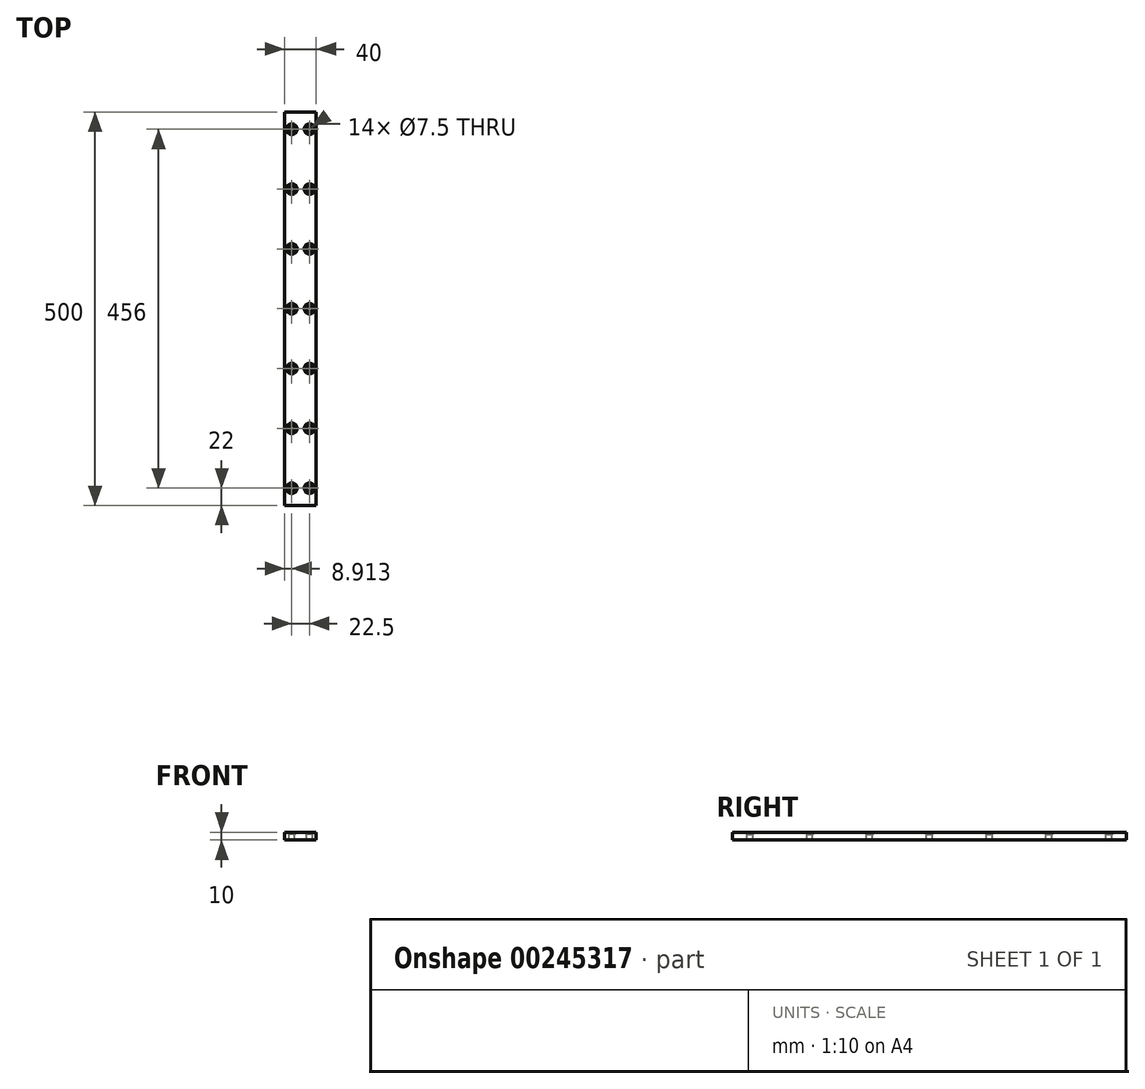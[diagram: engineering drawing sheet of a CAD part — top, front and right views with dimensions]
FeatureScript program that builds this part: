
annotation { "Feature Type Name" : "Feature", "Feature Type Description" : "" }
export const myFeature = defineFeature(function(context is Context, id is Id, definition is map)
    precondition{}
    {
        {
            var Q0;
            Q0=qCreatedBy(makeId("Front.planeOp"),FACE);
            var sketch = newSketch(context, id + "F0", { "sketchPlane" : qUnion([Q0])});
            skLineSegment(sketch, "E0.top", {"start": v(0, 434.89) * mm, "end": v(34.8, 434.89) * mm});
            skLineSegment(sketch, "E1.bottom", {"start": v(0, 0) * mm, "end": v(40, 0) * mm});
            skLineSegment(sketch, "E1.top", {"start": v(0, 10) * mm, "end": v(40, 10) * mm});
            skLineSegment(sketch, "E1.left", {"start": v(0, 0) * mm, "end": v(0, 10) * mm});
            skLineSegment(sketch, "E1.right", {"start": v(40, 0) * mm, "end": v(40, 10) * mm});
            skSolve(sketch);
        }
        {
            var Q0;
            Q0 = qSketchRegion(id + "F0", true);
            extrude(context, id + "F1", {"entities" : qUnion([Q0]), "depth" : 500 * mm, "offsetDistance" : 25 * mm});
        }
        {
            var Q0;
            Q0=makeQuery(id+"F1.opExtrude","SWEPT_FACE",FACE,{"disambiguationData":[OSD([sQuery(id+"F0.wireOp",EDGE,"E1.top")])]});
            var sketch = newSketch(context, id + "F2", { "sketchPlane" : qUnion([Q0])});
            skPoint(sketch, "E2", {"position": v(8.91, -22) * mm});
            skPoint(sketch, "E3.0.1.0", {"position": v(8.91, -98) * mm});
            skPoint(sketch, "E3.0.2.0", {"position": v(8.91, -174) * mm});
            skPoint(sketch, "E3.0.3.0", {"position": v(8.91, -250) * mm});
            skPoint(sketch, "E3.0.4.0", {"position": v(8.91, -326) * mm});
            skPoint(sketch, "E3.0.5.0", {"position": v(8.91, -402) * mm});
            skPoint(sketch, "E3.0.6.0", {"position": v(8.91, -478) * mm});
            skPoint(sketch, "E3.1.0.0", {"position": v(31.41, -22) * mm});
            skPoint(sketch, "E3.1.1.0", {"position": v(31.41, -98) * mm});
            skPoint(sketch, "E3.1.2.0", {"position": v(31.41, -174) * mm});
            skPoint(sketch, "E3.1.3.0", {"position": v(31.41, -250) * mm});
            skPoint(sketch, "E3.1.4.0", {"position": v(31.41, -326) * mm});
            skPoint(sketch, "E3.1.5.0", {"position": v(31.41, -402) * mm});
            skPoint(sketch, "E3.1.6.0", {"position": v(31.41, -478) * mm});
            skLineSegment(sketch, "E3.direction1", {"start": v(8.91, -22) * mm, "end": v(31.41, -22) * mm, "construction": true});
            skLineSegment(sketch, "E3.direction2", {"start": v(8.91, -22) * mm, "end": v(8.91, -98) * mm, "construction": true});
            skSolve(sketch);
        }
        {
            var Q0;
            Q0=sQuery(id+"F2.wireOp",VERTEX,"E3.0.6.0");
            var Q1;
            Q1=sQuery(id+"F2.wireOp",VERTEX,"E3.1.6.0");
            var Q2;
            Q2=sQuery(id+"F2.wireOp",VERTEX,"E3.0.5.0");
            var Q3;
            Q3=sQuery(id+"F2.wireOp",VERTEX,"E3.1.5.0");
            var Q4;
            Q4=sQuery(id+"F2.wireOp",VERTEX,"E3.1.4.0");
            var Q5;
            Q5=sQuery(id+"F2.wireOp",VERTEX,"E3.0.3.0");
            var Q6;
            Q6=sQuery(id+"F2.wireOp",VERTEX,"E3.0.2.0");
            var Q7;
            Q7=sQuery(id+"F2.wireOp",VERTEX,"E3.1.2.0");
            var Q8;
            Q8=sQuery(id+"F2.wireOp",VERTEX,"E3.0.4.0");
            var Q9;
            Q9=sQuery(id+"F2.wireOp",VERTEX,"E3.0.1.0");
            var Q10;
            Q10=sQuery(id+"F2.wireOp",VERTEX,"E3.1.1.0");
            var Q11;
            Q11=sQuery(id+"F2.wireOp",VERTEX,"E3.direction1.start");
            var Q12;
            Q12=sQuery(id+"F2.wireOp",VERTEX,"E3.1.0.0");
            var Q13;
            Q13=sQuery(id+"F2.wireOp",VERTEX,"E3.1.3.0");
            var Q14;
            Q14=makeQuery(id+"F1.opExtrude","SWEPT_BODY",BODY,{"disambiguationData":[OSD([sQuery(id+"F0.wireOp",EDGE,"E1.bottom"),sQuery(id+"F0.wireOp",EDGE,"E1.top"),sQuery(id+"F0.wireOp",EDGE,"E1.left"),sQuery(id+"F0.wireOp",EDGE,"E1.right")])]});
            hole(context, id + "F3", {"style" : HoleStyle.C_SINK, "endStyle" : HoleEndStyle.THROUGH, "holeDiameter" : 7.5 * mm, "cSinkDiameter" : 13.44 * mm, "cSinkAngle" : 90 * degree, "majorDiameter" : 6 * mm, "isTappedThrough" : true, "tappedDepth" : 31.25 * mm, "tapClearance" : 3, "startFromSketch" : true, "locations" : qUnion([Q0, Q1, Q2, Q3, Q4, Q5, Q6, Q7, Q8, Q9, Q10, Q11, Q12, Q13]), "scope" : qUnion([Q14])});
        }
    });
